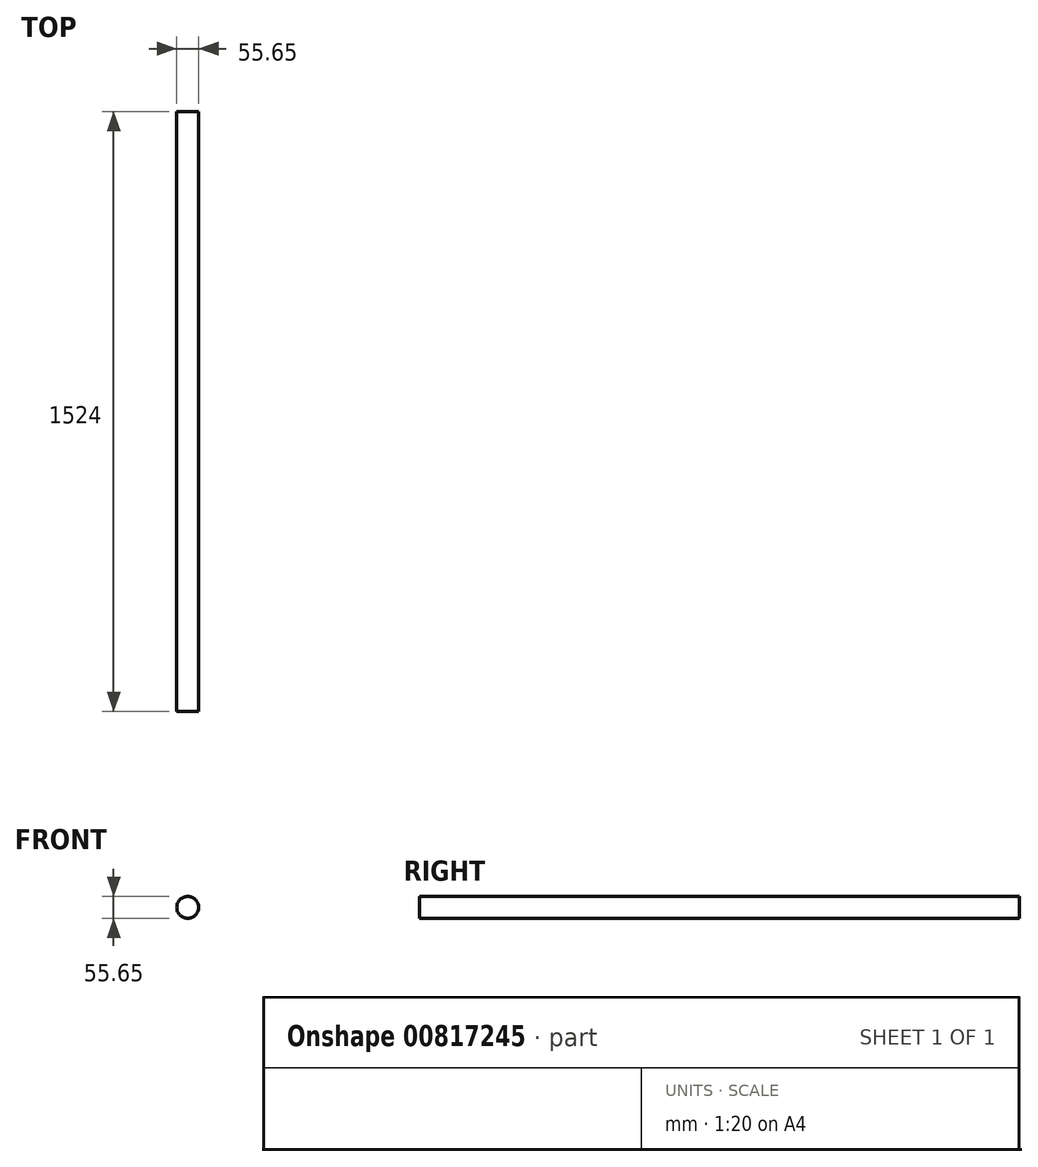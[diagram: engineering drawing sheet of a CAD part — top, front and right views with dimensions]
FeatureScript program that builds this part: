
annotation { "Feature Type Name" : "Feature", "Feature Type Description" : "" }
export const myFeature = defineFeature(function(context is Context, id is Id, definition is map)
    precondition{}
    {
        {
            var Q0;
            Q0=qCreatedBy(makeId("Front.planeOp"),FACE);
            var sketch = newSketch(context, id + "F0", { "sketchPlane" : qUnion([Q0])});
            skCircle(sketch, "E0", {"center": v(-46.4, -58.94) * mm, "radius": 27.83 * mm});
            skSolve(sketch);
        }
        {
            var Q0;
            Q0 = qSketchRegion(id + "F0", true);
            extrude(context, id + "F1", {"entities" : qUnion([Q0]), "depth" : 1524 * mm, "offsetDistance" : 25.4 * mm});
        }
    });
